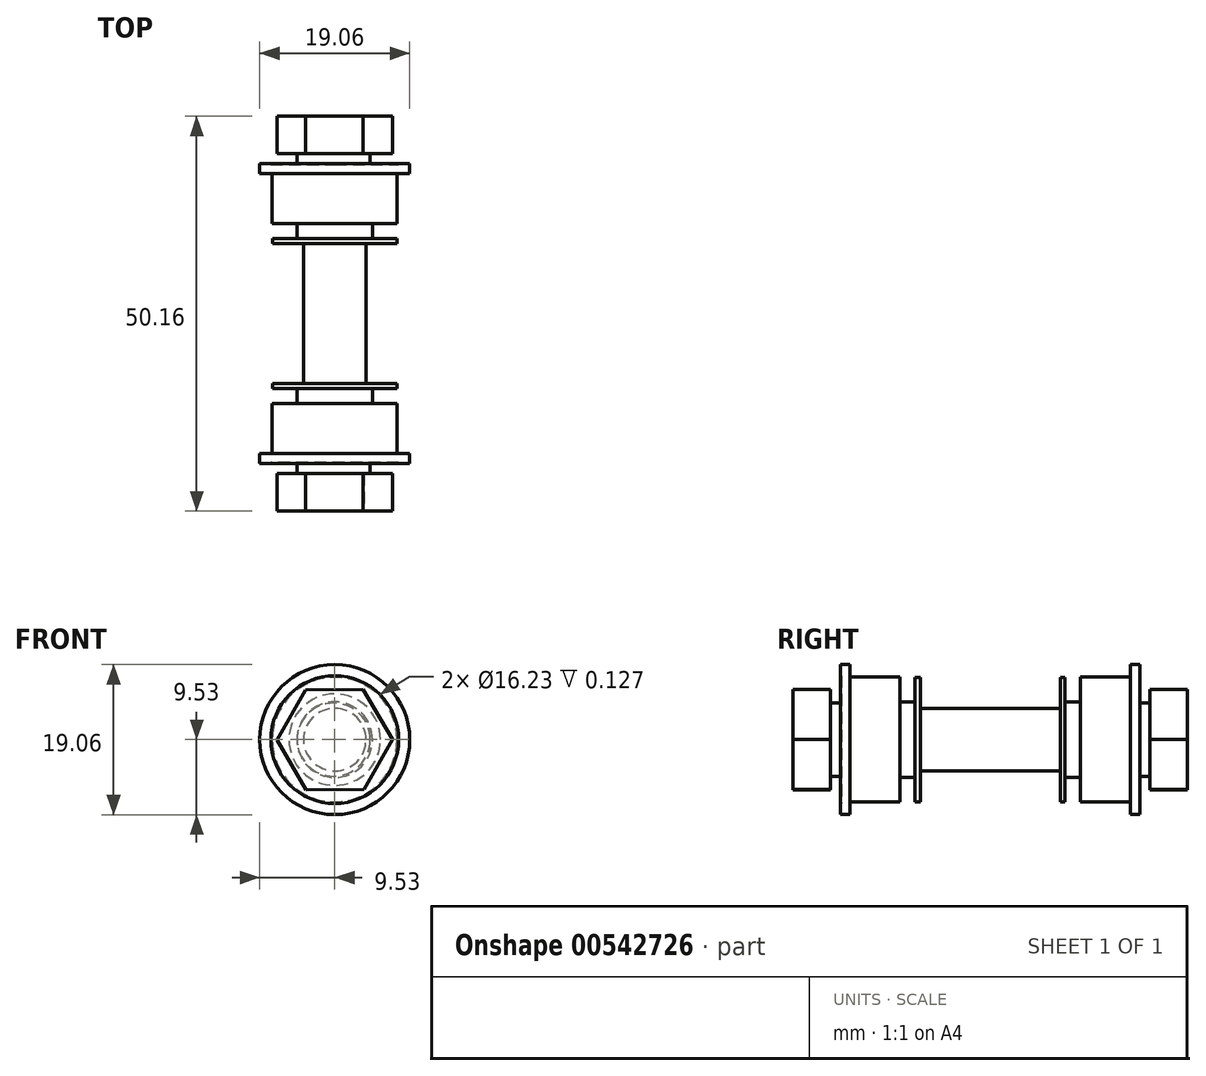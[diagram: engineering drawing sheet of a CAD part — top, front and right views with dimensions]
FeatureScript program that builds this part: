
annotation { "Feature Type Name" : "Feature", "Feature Type Description" : "" }
export const myFeature = defineFeature(function(context is Context, id is Id, definition is map)
    precondition{}
    {
        {
            var Q0;
            Q0=qCreatedBy(makeId("Front.planeOp"),FACE);
            var sketch = newSketch(context, id + "F0", { "sketchPlane" : qUnion([Q0])});
            skCircle(sketch, "E0.cCircle", {"center": v(0, 0) * mm, "radius": 6.35 * mm, "construction": true});
            skLineSegment(sketch, "E0.0", {"start": v(-7.33, -0.04) * mm, "end": v(-3.7, 6.33) * mm});
            skLineSegment(sketch, "E0.1", {"start": v(-3.7, 6.33) * mm, "end": v(3.63, 6.37) * mm});
            skLineSegment(sketch, "E0.2", {"start": v(3.63, 6.37) * mm, "end": v(7.33, 0.04) * mm});
            skLineSegment(sketch, "E0.3", {"start": v(7.33, 0.04) * mm, "end": v(3.7, -6.33) * mm});
            skLineSegment(sketch, "E0.4", {"start": v(3.7, -6.33) * mm, "end": v(-3.63, -6.37) * mm});
            skLineSegment(sketch, "E0.5", {"start": v(-3.63, -6.37) * mm, "end": v(-7.33, -0.04) * mm});
            skPoint(sketch, "E0.0.midPoint", {"position": v(-5.52, 3.14) * mm});
            skSolve(sketch);
        }
        {
            var Q0;
            Q0 = qSketchRegion(id + "F0", true);
            extrude(context, id + "F1", {"entities" : qUnion([Q0]), "depth" : 4.76 * mm, "offsetDistance" : 25.4 * mm});
        }
        {
            var Q0;
            Q0=makeQuery(id+"F1.opExtrude","CAP_FACE",FACE,{"disambiguationData":[OSD([sQuery(id+"F0.wireOp",EDGE,"E0.0"),sQuery(id+"F0.wireOp",EDGE,"E0.1"),sQuery(id+"F0.wireOp",EDGE,"E0.2"),sQuery(id+"F0.wireOp",EDGE,"E0.3"),sQuery(id+"F0.wireOp",EDGE,"E0.4"),sQuery(id+"F0.wireOp",EDGE,"E0.5")])],"isStart":false});
            var sketch = newSketch(context, id + "F2", { "sketchPlane" : qUnion([Q0])});
            skCircle(sketch, "E1", {"center": v(0, 0) * mm, "radius": 3.97 * mm});
            skSolve(sketch);
        }
        {
            var Q0;
            Q0 = qSketchRegion(id + "F2", true);
            extrude(context, id + "F3", {"entities" : qUnion([Q0]), "operationType" : NewBodyOperationType.ADD, "depth" : 20.32 * mm, "offsetDistance" : 25.4 * mm});
        }
        {
            var Q0;
            Q0=makeQuery(id+"F1.opExtrude","CAP_FACE",FACE,{"disambiguationData":[OSD([sQuery(id+"F0.wireOp",EDGE,"E0.0"),sQuery(id+"F0.wireOp",EDGE,"E0.1"),sQuery(id+"F0.wireOp",EDGE,"E0.2"),sQuery(id+"F0.wireOp",EDGE,"E0.3"),sQuery(id+"F0.wireOp",EDGE,"E0.4"),sQuery(id+"F0.wireOp",EDGE,"E0.5")])],"isStart":false});
            var sketch = newSketch(context, id + "F4", { "sketchPlane" : qUnion([Q0])});
            skCircle(sketch, "E2", {"center": v(-0.13, 0) * mm, "radius": 4.65 * mm});
            skSolve(sketch);
        }
        {
            var Q0;
            Q0 = qSketchRegion(id + "F4", true);
            extrude(context, id + "F5", {"entities" : qUnion([Q0]), "operationType" : NewBodyOperationType.ADD, "depth" : 1.27 * mm, "offsetDistance" : 25.4 * mm});
        }
        {
            var Q0;
            Q0=makeQuery(id+"F5.opExtrude","CAP_FACE",FACE,{"disambiguationData":[OSD([sQuery(id+"F4.wireOp",EDGE,"E2")])],"isStart":false});
            var sketch = newSketch(context, id + "F6", { "sketchPlane" : qUnion([Q0])});
            skCircle(sketch, "E3", {"center": v(0, 0) * mm, "radius": 9.53 * mm});
            skSolve(sketch);
        }
        {
            var Q0;
            Q0 = qSketchRegion(id + "F6", true);
            extrude(context, id + "F7", {"entities" : qUnion([Q0]), "operationType" : NewBodyOperationType.ADD, "depth" : 1.27 * mm, "offsetDistance" : 25.4 * mm});
        }
        {
            var Q0;
            Q0=makeQuery(id+"F7.opExtrude","CAP_FACE",FACE,{"disambiguationData":[OSD([sQuery(id+"F6.wireOp",EDGE,"E3")])],"isStart":true});
            var sketch = newSketch(context, id + "F8", { "sketchPlane" : qUnion([Q0])});
            skCircle(sketch, "E4", {"center": v(0, 0) * mm, "radius": 8.12 * mm});
            skCircle(sketch, "E5", {"center": v(0, 0) * mm, "radius": 5.81 * mm});
            skSolve(sketch);
        }
        {
            var Q0;
            Q0 = qSketchRegion(id + "F8", true);
            extrude(context, id + "F9", {"entities" : qUnion([Q0]), "operationType" : NewBodyOperationType.REMOVE, "oppositeDirection" : true, "depth" : 0.13 * mm, "offsetDistance" : 25.4 * mm});
        }
        {
            var Q0;
            Q0=makeQuery(id+"F7.opExtrude","CAP_FACE",FACE,{"disambiguationData":[OSD([sQuery(id+"F6.wireOp",EDGE,"E3")])],"isStart":false});
            var sketch = newSketch(context, id + "F10", { "sketchPlane" : qUnion([Q0])});
            skCircle(sketch, "E6", {"center": v(0, 0) * mm, "radius": 7.94 * mm});
            skSolve(sketch);
        }
        {
            var Q0;
            Q0 = qSketchRegion(id + "F10", true);
            extrude(context, id + "F11", {"entities" : qUnion([Q0]), "operationType" : NewBodyOperationType.ADD, "depth" : 6.35 * mm, "offsetDistance" : 25.4 * mm});
        }
        {
            var Q0;
            Q0=makeQuery(id+"F11.opExtrude","CAP_FACE",FACE,{"disambiguationData":[OSD([sQuery(id+"F10.wireOp",EDGE,"E6")])],"isStart":false});
            var sketch = newSketch(context, id + "F12", { "sketchPlane" : qUnion([Q0])});
            skCircle(sketch, "E7", {"center": v(0, 0) * mm, "radius": 4.8 * mm});
            skSolve(sketch);
        }
        {
            var Q0;
            Q0 = qSketchRegion(id + "F12", true);
            extrude(context, id + "F13", {"entities" : qUnion([Q0]), "operationType" : NewBodyOperationType.ADD, "depth" : 1.9 * mm, "offsetDistance" : 25.4 * mm});
        }
        {
            var Q0;
            Q0=makeQuery(id+"F13.opExtrude","CAP_FACE",FACE,{"disambiguationData":[OSD([sQuery(id+"F12.wireOp",EDGE,"E7")])],"isStart":false});
            var sketch = newSketch(context, id + "F14", { "sketchPlane" : qUnion([Q0])});
            skCircle(sketch, "E8", {"center": v(0, 0) * mm, "radius": 7.92 * mm});
            skSolve(sketch);
        }
        {
            var Q0;
            Q0 = qSketchRegion(id + "F14", true);
            extrude(context, id + "F15", {"entities" : qUnion([Q0]), "operationType" : NewBodyOperationType.ADD, "depth" : 0.64 * mm, "offsetDistance" : 25.4 * mm});
        }
        {
            var Q0;
            Q0=makeQuery(id+"F1.opExtrude","SWEPT_BODY",BODY,{"disambiguationData":[OSD([sQuery(id+"F0.wireOp",EDGE,"E0.0"),sQuery(id+"F0.wireOp",EDGE,"E0.1"),sQuery(id+"F0.wireOp",EDGE,"E0.2"),sQuery(id+"F0.wireOp",EDGE,"E0.3"),sQuery(id+"F0.wireOp",EDGE,"E0.4"),sQuery(id+"F0.wireOp",EDGE,"E0.5")])]});
            var Q1;
            Q1=makeQuery(id+"F3.opExtrude","CAP_FACE",FACE,{"disambiguationData":[OSD([sQuery(id+"F2.wireOp",EDGE,"E1")])],"isStart":false});
            mirror(context, id + "F16", {"operationType" : NewBodyOperationType.ADD, "entities" : qUnion([Q0]), "mirrorPlane" : qUnion([Q1])});
        }
    });
